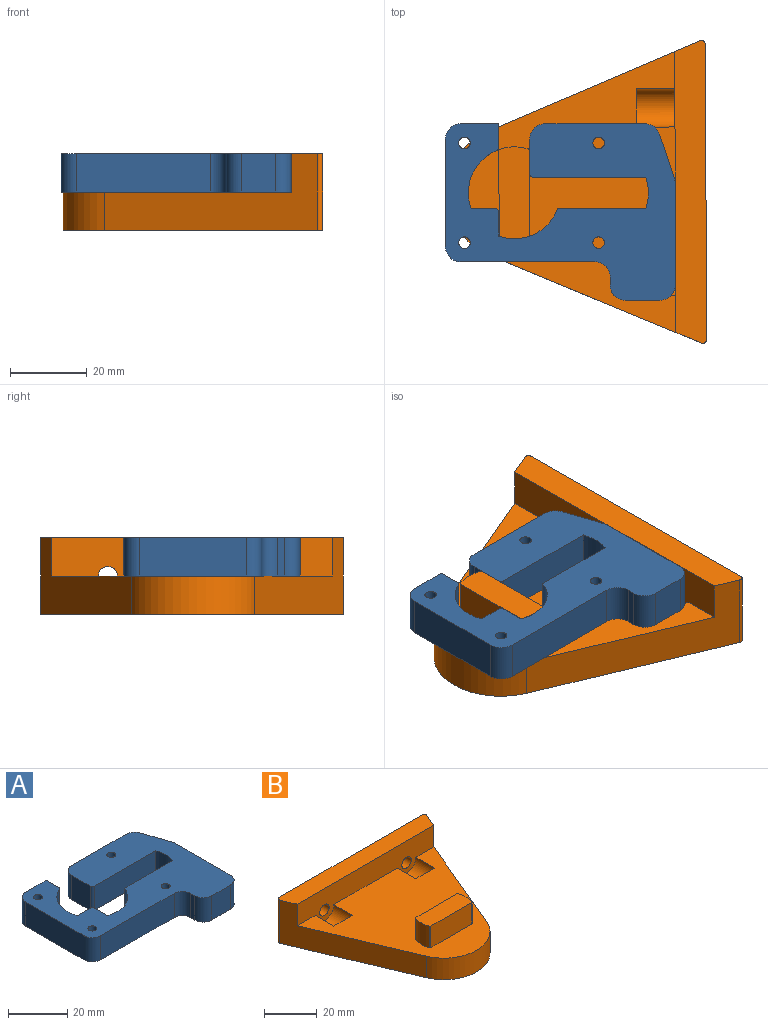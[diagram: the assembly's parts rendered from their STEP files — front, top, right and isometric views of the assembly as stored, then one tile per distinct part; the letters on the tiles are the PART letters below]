
ASSEMBLY  parts=2 mates=1
PART A: 38 faces, bbox 60x46x10 mm
  f0: cylinder r=12mm len=15.11mm, axis (0,0,-1), area 181.9mm2, adj f16,f17,f18,f27
  f1: plane 10x6.02mm, normal (1,0,0), area 60.2mm2, adj f2,f17,f18,f27
  f2: plane 10x9.95mm, normal (0,1,0), area 99.5mm2, adj f1,f17,f18,f30
  f3: plane 28x10mm, normal (-1,0,0), area 280mm2, adj f17,f18,f30,f31
  f4: plane 35x10mm, normal (0,-1,0), area 350mm2, adj f17,f18,f31,f32
  f5: plane 10x2mm, normal (-1,0,0), area 20mm2, adj f17,f18,f32,f33
  f6: plane 10x9mm, normal (0,-1,0), area 90mm2, adj f17,f18,f33,f34
  f7: plane 26.35x10mm, normal (1,0,0), area 263.5mm2, adj f17,f18,f34,f35
  f8: plane 11.65x10mm, normal (0.95,0.32,0), area 122.8mm2, adj f17,f18,f35,f36
  f9: plane 26.12x10mm, normal (0,1,0), area 261.2mm2, adj f17,f18,f36,f37
  f10: plane 10x8.95mm, normal (-1,0,0), area 89.5mm2, adj f17,f18,f28,f37
  f11: plane 29.3x10mm, normal (0,-1,0), area 293mm2, adj f12,f17,f18,f28
  f12: cylinder r=12mm len=10mm, axis (0,0,-1), area 82.6mm2, adj f11,f13,f17,f18
  f13: plane 23x10mm, normal (0,1,0), area 230mm2, adj f12,f14,f17,f18
  f14: cylinder r=12mm len=15.35mm, axis (0,0,-1), area 188.5mm2, adj f13,f15,f17,f18
  f15: plane 10x6.25mm, normal (1,0,0), area 62.5mm2, adj f14,f17,f18,f29
  f16: plane 10x6.25mm, normal (0,1,0), area 62.5mm2, adj f0,f17,f18,f29
  f17: plane 60x46mm, normal (0,0,1), area 1628.3mm2, adj f0,f1,f2,f3,f4,f5,f6,f7
  f18: plane 60x46mm, normal (0,0,-1), area 1543.5mm2, adj f0,f1,f2,f3,f4,f5,f6,f7
  f19: cylinder r=1.5mm len=8.5mm, axis (0,0,-1), area 80.1mm2, adj f17,f20
  f20: cone r=1.5mm half-angle=45deg, axis (0,0,-1), area 30mm2, adj f18,f19
  f21: cylinder r=1.5mm len=8.5mm, axis (0,0,-1), area 80.1mm2, adj f17,f22
  f22: cone r=1.5mm half-angle=45deg, axis (0,0,-1), area 30mm2, adj f18,f21
  f23: cylinder r=1.5mm len=8.5mm, axis (0,0,-1), area 80.1mm2, adj f17,f24
  f24: cone r=1.5mm half-angle=45deg, axis (0,0,-1), area 30mm2, adj f18,f23
  f25: cylinder r=1.5mm len=8.5mm, axis (0,0,-1), area 80.1mm2, adj f17,f26
  f26: cone r=1.5mm half-angle=45deg, axis (0,0,-1), area 30mm2, adj f18,f25
  f27: cylinder r=1mm len=10mm, axis (0,0,-1), area 11.7mm2, adj f0,f1,f17,f18
  f28: cylinder r=1mm len=10mm, axis (0,0,-1), area 15.7mm2, adj f10,f11,f17,f18
  f29: cylinder r=1mm len=10mm, axis (0,0,1), area 15.7mm2, adj f15,f16,f17,f18
  f30: cylinder r=4mm len=10mm, axis (0,0,1), area 62.8mm2, adj f2,f3,f17,f18
  f31: cylinder r=4mm len=10mm, axis (0,0,-1), area 62.8mm2, adj f3,f4,f17,f18
  f32: cylinder r=4mm len=10mm, axis (0,0,-1), area 62.8mm2, adj f4,f5,f17,f18
  f33: cylinder r=4mm len=10mm, axis (0,0,-1), area 62.8mm2, adj f5,f6,f17,f18
  f34: cylinder r=4mm len=10mm, axis (0,0,-1), area 62.8mm2, adj f6,f7,f17,f18
  f35: cylinder r=4mm len=10mm, axis (0,0,-1), area 12.9mm2, adj f7,f8,f17,f18
  f36: cylinder r=4mm len=10mm, axis (0,0,-1), area 50mm2, adj f8,f9,f17,f18
  f37: cylinder r=4mm len=10mm, axis (0,0,1), area 62.8mm2, adj f9,f10,f17,f18
PART B: 25 faces, bbox 79x67.5x20 mm
  f0: plane 73.27x59.5mm, normal (0,0,1), area 2435.7mm2, adj f1,f3,f4,f5,f7,f8,f9,f10
  f1: plane 73.27x15mm, normal (0,-1,0), area 772mm2, adj f0,f3,f5,f12,f13,f14,f21,f23
  f2: plane 76.99x20mm, normal (0,1,0), area 1500.5mm2, adj f6,f12,f13,f14,f15,f16
  f3: plane 55.39x23.28mm, normal (-0.92,-0.39,0), area 672.6mm2, adj f0,f1,f4,f6,f12,f15
  f4: cylinder r=17.5mm len=32.27mm, axis (0,0,-1), area 410.5mm2, adj f0,f3,f5,f6
  f5: plane 55.39x23.28mm, normal (0.92,-0.39,0), area 672.6mm2, adj f0,f1,f4,f6,f12,f16
  f6: plane 78.99x67.5mm, normal (0,0,-1), area 3436mm2, adj f2,f3,f4,f5,f15,f16
  f7: plane 21.91x10mm, normal (0,1,0), area 219.1mm2, adj f0,f11,f17,f18
  f8: cylinder r=12mm len=10mm, axis (0,0,-1), area 74.2mm2, adj f0,f11,f18,f20
  f9: plane 21.91x10mm, normal (0,-1,0), area 219.1mm2, adj f0,f11,f19,f20
  f10: cylinder r=12mm len=10mm, axis (0,0,-1), area 74.2mm2, adj f0,f11,f17,f19
  f11: plane 24x8mm, normal (0,0,1), area 188.3mm2, adj f7,f8,f9,f10,f17,f18,f19,f20
  f12: plane 78.99x8mm, normal (0,0,1), area 612.1mm2, adj f1,f2,f3,f5,f15,f16
  f13: cylinder r=2.5mm len=8mm, axis (0,1,0), area 125.7mm2, adj f1,f2
  f14: cylinder r=2.5mm len=8mm, axis (0,1,0), area 125.7mm2, adj f1,f2
  f15: cylinder r=1mm len=20mm, axis (0,0,1), area 39.4mm2, adj f2,f3,f6,f12
  f16: cylinder r=1mm len=20mm, axis (0,0,1), area 39.4mm2, adj f2,f5,f6,f12
  f17: cylinder r=0.5mm len=10mm, axis (0,0,-1), area 6.3mm2, adj f0,f7,f10,f11
  f18: cylinder r=0.5mm len=10mm, axis (0,0,-1), area 6.3mm2, adj f0,f7,f8,f11
  f19: cylinder r=0.5mm len=10mm, axis (0,0,-1), area 6.3mm2, adj f0,f9,f10,f11
  f20: cylinder r=0.5mm len=10mm, axis (0,0,-1), area 6.3mm2, adj f0,f8,f9,f11
  f21: cylinder r=5mm len=10mm, axis (0,1,0), area 157.1mm2, adj f0,f1,f22
  f22: plane 10x5mm, normal (0,1,0), area 39.3mm2, adj f0,f21
  f23: cylinder r=5mm len=10mm, axis (0,1,0), area 157.1mm2, adj f0,f1,f24
  f24: plane 10x5mm, normal (0,1,0), area 39.3mm2, adj f0,f23
PLACE A t=(18.55,131,13.91)mm
PLACE B rot(axis=(0,0,-1),89.7deg) t=(-18.92,235.87,3.91)mm
MATE revolute B.f4 <-> A.f0  axis (0,0,1) through (-19.2,144,23.91)mm
